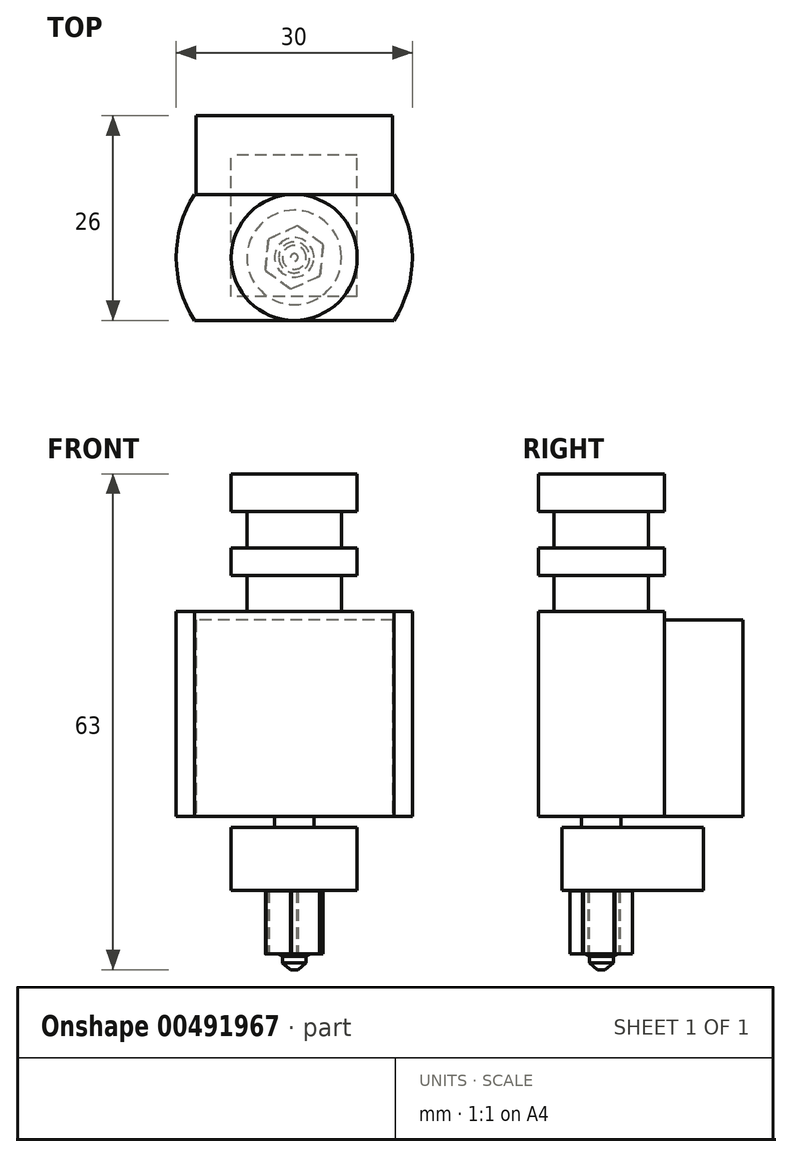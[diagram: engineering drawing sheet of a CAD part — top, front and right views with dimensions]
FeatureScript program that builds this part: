
annotation { "Feature Type Name" : "Feature", "Feature Type Description" : "" }
export const myFeature = defineFeature(function(context is Context, id is Id, definition is map)
    precondition{}
    {
        {
            var Q0;
            Q0=qCreatedBy(makeId("Front.planeOp"),FACE);
            var sketch = newSketch(context, id + "F0", { "sketchPlane" : qUnion([Q0])});
            skLineSegment(sketch, "E0", {"start": v(-0.47, -24.9) * mm, "end": v(-1.52, -24.04) * mm});
            skLineSegment(sketch, "E1", {"start": v(-1.52, -24.04) * mm, "end": v(-1.52, -23.2) * mm});
            skLineSegment(sketch, "E2", {"start": v(-1.52, -23.2) * mm, "end": v(-1.97, -22.92) * mm});
            skLineSegment(sketch, "E3", {"start": v(-1.97, -22.92) * mm, "end": v(-4, -22.9) * mm});
            skLineSegment(sketch, "E4", {"start": v(-4, -22.9) * mm, "end": v(-4, -14.9) * mm});
            skLineSegment(sketch, "E5", {"start": v(-4, -14.9) * mm, "end": v(-2.5, -14.9) * mm});
            skLineSegment(sketch, "E6", {"start": v(-2.5, -14.9) * mm, "end": v(-2.5, -5.4) * mm});
            skLineSegment(sketch, "E7", {"start": v(-2.5, -5.4) * mm, "end": v(-15, -5.4) * mm});
            skLineSegment(sketch, "E8", {"start": v(-15, -5.4) * mm, "end": v(-15, 20.6) * mm});
            skLineSegment(sketch, "E9", {"start": v(-15, 20.6) * mm, "end": v(-6, 20.6) * mm});
            skLineSegment(sketch, "E10", {"start": v(-6, 20.6) * mm, "end": v(-6, 25.2) * mm});
            skLineSegment(sketch, "E11", {"start": v(-6, 25.2) * mm, "end": v(-8, 25.2) * mm});
            skLineSegment(sketch, "E12", {"start": v(-8, 25.2) * mm, "end": v(-8, 28.7) * mm});
            skLineSegment(sketch, "E13", {"start": v(-8, 28.7) * mm, "end": v(-6, 28.7) * mm});
            skLineSegment(sketch, "E14", {"start": v(-6, 28.7) * mm, "end": v(-6, 33.3) * mm});
            skLineSegment(sketch, "E15", {"start": v(-6, 33.3) * mm, "end": v(-8, 33.3) * mm});
            skLineSegment(sketch, "E16", {"start": v(-8, 33.3) * mm, "end": v(-8, 38.1) * mm});
            skLineSegment(sketch, "E17", {"start": v(0, -5.47) * mm, "end": v(0, 4.05) * mm, "construction": true});
            skLineSegment(sketch, "E18", {"start": v(0, 4.05) * mm, "end": v(0, 49.6) * mm, "construction": true});
            skLineSegment(sketch, "E19", {"start": v(-8, 38.1) * mm, "end": v(0, 38.1) * mm});
            skLineSegment(sketch, "E20", {"start": v(-0.47, -24.9) * mm, "end": v(0, -24.9) * mm});
            skLineSegment(sketch, "E21", {"start": v(0, -5.47) * mm, "end": v(0, -26.02) * mm});
            skLineSegment(sketch, "E22", {"start": v(0, -5.47) * mm, "end": v(0, 38.1) * mm});
            skSolve(sketch);
        }
        {
            var Q0;
            Q0=qSketchRegion(id+"F0",true);
            var Q1;
            Q1=sQuery(id+"F0.wireOp",EDGE,"E18");
            revolve(context, id + "F1", {"entities" : qUnion([Q0]), "axis" : qUnion([Q1]), "revolveType" : RevolveType.FULL});
        }
        {
            var Q0;
            Q0=makeQuery(id+"F1.opRevolve","SWEPT_FACE",FACE,{"disambiguationData":[OSD([sQuery(id+"F0.wireOp",EDGE,"E9")])]});
            var sketch = newSketch(context, id + "F2", { "sketchPlane" : qUnion([Q0])});
            skLineSegment(sketch, "E23.bottom", {"start": v(-15, 8) * mm, "end": v(15, 8) * mm});
            skLineSegment(sketch, "E23.top", {"start": v(-15, -8) * mm, "end": v(15, -8) * mm});
            skLineSegment(sketch, "E23.left", {"start": v(-15, 8) * mm, "end": v(-15, -8) * mm});
            skLineSegment(sketch, "E23.right", {"start": v(15, 8) * mm, "end": v(15, -8) * mm});
            skPoint(sketch, "E23.middle", {"position": v(0, 0) * mm});
            skLineSegment(sketch, "E24.bottom", {"start": v(18.55, -23.05) * mm, "end": v(-18.55, -23.05) * mm});
            skLineSegment(sketch, "E24.top", {"start": v(18.55, 23.05) * mm, "end": v(-18.55, 23.05) * mm});
            skLineSegment(sketch, "E24.left", {"start": v(18.55, -23.05) * mm, "end": v(18.55, 23.05) * mm});
            skLineSegment(sketch, "E24.right", {"start": v(-18.55, -23.05) * mm, "end": v(-18.55, 23.05) * mm});
            skSolve(sketch);
        }
        {
            var Q0;
            Q0=qSketchRegion(id+"F2",true);
            extrude(context, id + "F3", {"entities" : qUnion([Q0]), "operationType" : NewBodyOperationType.REMOVE, "oppositeDirection" : true, "depth" : 27.4 * mm});
        }
        {
            var Q0;
            Q0=qCreatedBy(makeId("Front.planeOp"),FACE);
            var sketch = newSketch(context, id + "F4", { "sketchPlane" : qUnion([Q0])});
            skLineSegment(sketch, "E25.0.0", {"start": v(-12.69, -5.4) * mm, "end": v(-12.69, 20.6) * mm});
            skLineSegment(sketch, "E25.0.1", {"start": v(-12.69, 20.6) * mm, "end": v(12.69, 20.6) * mm});
            skLineSegment(sketch, "E25.0.2", {"start": v(12.69, 20.6) * mm, "end": v(12.69, -5.4) * mm});
            skLineSegment(sketch, "E25.0.3", {"start": v(12.69, -5.4) * mm, "end": v(-12.69, -5.4) * mm});
            skLineSegment(sketch, "E26", {"start": v(-4, -22.9) * mm, "end": v(-4, -14.9) * mm});
            skLineSegment(sketch, "E27", {"start": v(4, -14.81) * mm, "end": v(4, -22.9) * mm});
            skLineSegment(sketch, "E28", {"start": v(-2.5, -14.9) * mm, "end": v(-2.5, -5.4) * mm});
            skLineSegment(sketch, "E29", {"start": v(2.5, -5.4) * mm, "end": v(2.5, -14.81) * mm});
            skLineSegment(sketch, "E30.bottom", {"start": v(8, -14.81) * mm, "end": v(-8, -14.81) * mm});
            skLineSegment(sketch, "E30.top", {"start": v(8, -6.81) * mm, "end": v(-8, -6.81) * mm});
            skLineSegment(sketch, "E30.left", {"start": v(8, -14.81) * mm, "end": v(8, -6.81) * mm});
            skLineSegment(sketch, "E30.right", {"start": v(-8, -14.81) * mm, "end": v(-8, -6.81) * mm});
            skPoint(sketch, "E30.middle", {"position": v(0, -10.81) * mm});
            skSolve(sketch);
        }
        {
            var Q0;
            {var subQ4=sQuery(id+"F4.wireOp",EDGE,"E30.left");Q0=makeQuery(id+"F4.imprint","IMPRINT",FACE,{"disambiguationData":[TD([[makeQuery(id+"F4.imprint","IMPRINT",EDGE,{"derivedFrom":subQ4}),1.0]])]});}
            var Q1;
            {var subQ5=sQuery(id+"F4.wireOp",EDGE,"E30.right");Q1=makeQuery(id+"F4.imprint","IMPRINT",FACE,{"disambiguationData":[TD([[makeQuery(id+"F4.imprint","IMPRINT",EDGE,{"derivedFrom":subQ5}),-1.0]])]});}
            var Q2;
            {var subQ0=sQuery(id+"F4.wireOp",EDGE,"E30.bottom");var subQ1=sQuery(id+"F4.wireOp",EDGE,"E28");var subQ2=makeQuery(id+"F4.imprint","INTERSECT",VERTEX,{"derivedFrom":[subQ1,subQ0]});Q2=makeQuery(id+"F4.imprint","IMPRINT",FACE,{"disambiguationData":[TD([[makeQuery(id+"F4.imprint","IMPRINT",EDGE,{"disambiguationData":[TD([[subQ2,-1.0]])],"derivedFrom":subQ1}),-1.0]])]});}
            extrude(context, id + "F5", {"entities" : qUnion([Q0, Q1, Q2]), "operationType" : NewBodyOperationType.ADD, "depth" : 5 * mm, "hasSecondDirection" : true, "secondDirectionOppositeDirection" : true, "secondDirectionDepth" : 13 * mm});
        }
        {
            var Q0;
            Q0=makeQuery(id+"F5.opExtrude","SWEPT_FACE",FACE,{"disambiguationData":[OSD([sQuery(id+"F4.wireOp",EDGE,"E30.bottom")])]});
            var sketch = newSketch(context, id + "F6", { "sketchPlane" : qUnion([Q0])});
            skCircle(sketch, "E31.cCircle", {"center": v(0, 0) * mm, "radius": 3.5 * mm, "construction": true});
            skLineSegment(sketch, "E31.0", {"start": v(0.4, -4.02) * mm, "end": v(-3.29, -2.35) * mm});
            skLineSegment(sketch, "E31.1", {"start": v(-3.29, -2.35) * mm, "end": v(-3.68, 1.67) * mm});
            skLineSegment(sketch, "E31.2", {"start": v(-3.68, 1.67) * mm, "end": v(-0.4, 4.02) * mm});
            skLineSegment(sketch, "E31.3", {"start": v(-0.4, 4.02) * mm, "end": v(3.29, 2.35) * mm});
            skLineSegment(sketch, "E31.4", {"start": v(3.29, 2.35) * mm, "end": v(3.68, -1.67) * mm});
            skLineSegment(sketch, "E31.5", {"start": v(3.68, -1.67) * mm, "end": v(0.4, -4.02) * mm});
            skPoint(sketch, "E31.0.midPoint", {"position": v(-1.44, -3.19) * mm});
            skCircle(sketch, "E32", {"center": v(0, 0) * mm, "radius": 5.91 * mm});
            skSolve(sketch);
        }
        {
            var Q0;
            Q0=qSketchRegion(id+"F6",true);
            extrude(context, id + "F7", {"entities" : qUnion([Q0]), "operationType" : NewBodyOperationType.REMOVE, "depth" : 25 * mm});
        }
        {
            var Q0;
            Q0=makeQuery(id+"F3.boolean.opBoolean","COPY",FACE,{"derivedFrom":makeQuery(id+"F3.opExtrude","SWEPT_FACE",FACE,{"disambiguationData":[OSD([sQuery(id+"F2.wireOp",EDGE,"E23.bottom")])]})});
            var sketch = newSketch(context, id + "F8", { "sketchPlane" : qUnion([Q0])});
            skLineSegment(sketch, "E33.0.0", {"start": v(12.69, -5.4) * mm, "end": v(12.69, 20.6) * mm});
            skLineSegment(sketch, "E33.0.1", {"start": v(12.69, 20.6) * mm, "end": v(-12.69, 20.6) * mm});
            skLineSegment(sketch, "E33.0.2", {"start": v(-12.69, 20.6) * mm, "end": v(-12.69, -5.4) * mm});
            skLineSegment(sketch, "E33.0.3", {"start": v(-12.69, -5.4) * mm, "end": v(12.69, -5.4) * mm});
            skLineSegment(sketch, "E34.bottom", {"start": v(-12.5, 19.54) * mm, "end": v(12.5, 19.54) * mm});
            skLineSegment(sketch, "E34.top", {"start": v(-12.5, -5.46) * mm, "end": v(12.5, -5.46) * mm});
            skLineSegment(sketch, "E34.left", {"start": v(-12.5, 19.54) * mm, "end": v(-12.5, -5.46) * mm});
            skLineSegment(sketch, "E34.right", {"start": v(12.5, 19.54) * mm, "end": v(12.5, -5.46) * mm});
            skPoint(sketch, "E34.middle", {"position": v(0, 7.04) * mm});
            skSolve(sketch);
        }
        {
            var Q0;
            {var subQ5=sQuery(id+"F8.wireOp",EDGE,"E34.bottom");Q0=makeQuery(id+"F8.imprint","IMPRINT",FACE,{"disambiguationData":[TD([[makeQuery(id+"F8.imprint","IMPRINT",EDGE,{"derivedFrom":subQ5}),-1.0]])]});}
            extrude(context, id + "F9", {"entities" : qUnion([Q0]), "operationType" : NewBodyOperationType.ADD, "depth" : 10 * mm});
        }
    });
